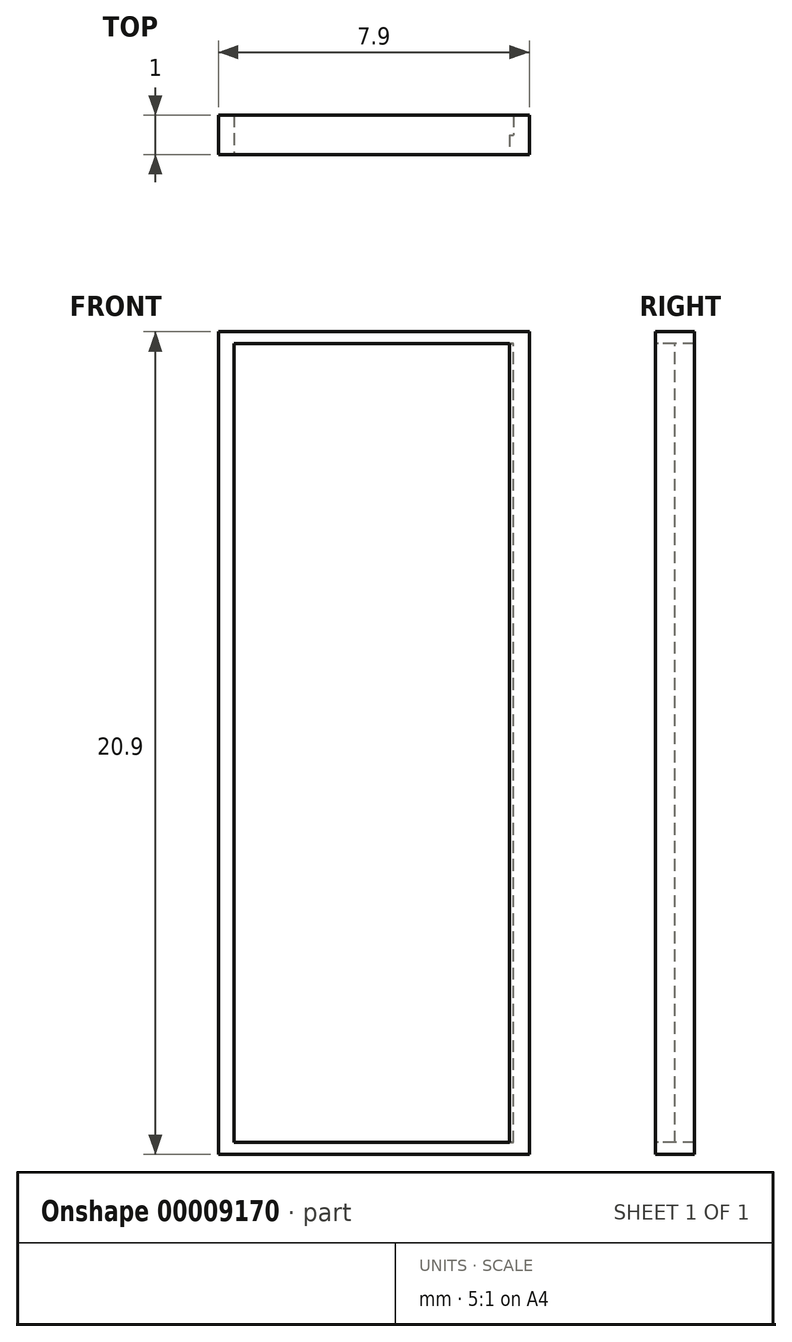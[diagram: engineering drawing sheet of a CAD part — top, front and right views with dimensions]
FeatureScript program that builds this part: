
annotation { "Feature Type Name" : "Feature", "Feature Type Description" : "" }
export const myFeature = defineFeature(function(context is Context, id is Id, definition is map)
    precondition{}
    {
        {
            var Q0;
            Q0=qCreatedBy(makeId("Front.planeOp"),FACE);
            var sketch = newSketch(context, id + "F0", { "sketchPlane" : qUnion([Q0])});
            skLineSegment(sketch, "E0.rect.bottom", {"start": v(3.95, 10.45) * mm, "end": v(-3.95, 10.45) * mm});
            skLineSegment(sketch, "E0.rect.top", {"start": v(3.95, -10.45) * mm, "end": v(-3.95, -10.45) * mm});
            skLineSegment(sketch, "E0.rect.left", {"start": v(3.95, 10.45) * mm, "end": v(3.95, -10.45) * mm});
            skLineSegment(sketch, "E0.rect.right", {"start": v(-3.95, 10.45) * mm, "end": v(-3.95, -10.45) * mm});
            skPoint(sketch, "E0.rect.middle", {"position": v(0, 0) * mm});
            skSolve(sketch);
        }
        {
            var Q0;
            Q0 = qSketchRegion(id + "F0", true);
            extrude(context, id + "F1", {"entities" : qUnion([Q0]), "oppositeDirection" : true, "depth" : 1 * mm});
        }
        {
            var Q0;
            Q0=makeQuery(id+"F1.opExtrude","CAP_FACE",FACE,{"disambiguationData":[OSD([sQuery(id+"F0.wireOp",EDGE,"E0.rect.bottom"),sQuery(id+"F0.wireOp",EDGE,"E0.rect.top"),sQuery(id+"F0.wireOp",EDGE,"E0.rect.left"),sQuery(id+"F0.wireOp",EDGE,"E0.rect.right")])],"isStart":true});
            var sketch = newSketch(context, id + "F2", { "sketchPlane" : qUnion([Q0])});
            skLineSegment(sketch, "E1.rect.bottom", {"start": v(3.55, 10.15) * mm, "end": v(-3.55, 10.15) * mm});
            skLineSegment(sketch, "E1.rect.top", {"start": v(3.55, -10.15) * mm, "end": v(-3.55, -10.15) * mm});
            skLineSegment(sketch, "E1.rect.left", {"start": v(3.55, 10.15) * mm, "end": v(3.55, -10.15) * mm});
            skLineSegment(sketch, "E1.rect.right", {"start": v(-3.55, 10.15) * mm, "end": v(-3.55, -10.15) * mm});
            skPoint(sketch, "E1.rect.middle", {"position": v(0, 0) * mm});
            skSolve(sketch);
        }
        {
            var Q0;
            Q0 = qSketchRegion(id + "F2", true);
            extrude(context, id + "F3", {"entities" : qUnion([Q0]), "operationType" : NewBodyOperationType.REMOVE, "oppositeDirection" : true, "depth" : 25 * mm});
        }
        {
            var Q0;
            Q0=makeQuery(id+"F3.boolean.opBoolean","COPY",FACE,{"derivedFrom":makeQuery(id+"F3.opExtrude","SWEPT_FACE",FACE,{"disambiguationData":[OSD([sQuery(id+"F2.wireOp",EDGE,"E1.rect.left")])]})});
            var sketch = newSketch(context, id + "F4", { "sketchPlane" : qUnion([Q0])});
            skLineSegment(sketch, "E2", {"start": v(-0.5, -10.15) * mm, "end": v(-0.5, 10.15) * mm});
            skSolve(sketch);
        }
        {
            var Q0;
            {var subQ2=sQuery(id+"F4.wireOp",EDGE,"E2");Q0=makeQuery(id+"F4.imprint","IMPRINT",FACE,{"disambiguationData":[TD([[makeQuery(id+"F4.imprint","IMPRINT",EDGE,{"derivedFrom":subQ2}),-1.0]])]});}
            extrude(context, id + "F5", {"entities" : qUnion([Q0]), "operationType" : NewBodyOperationType.ADD, "depth" : 0.1 * mm});
        }
    });
